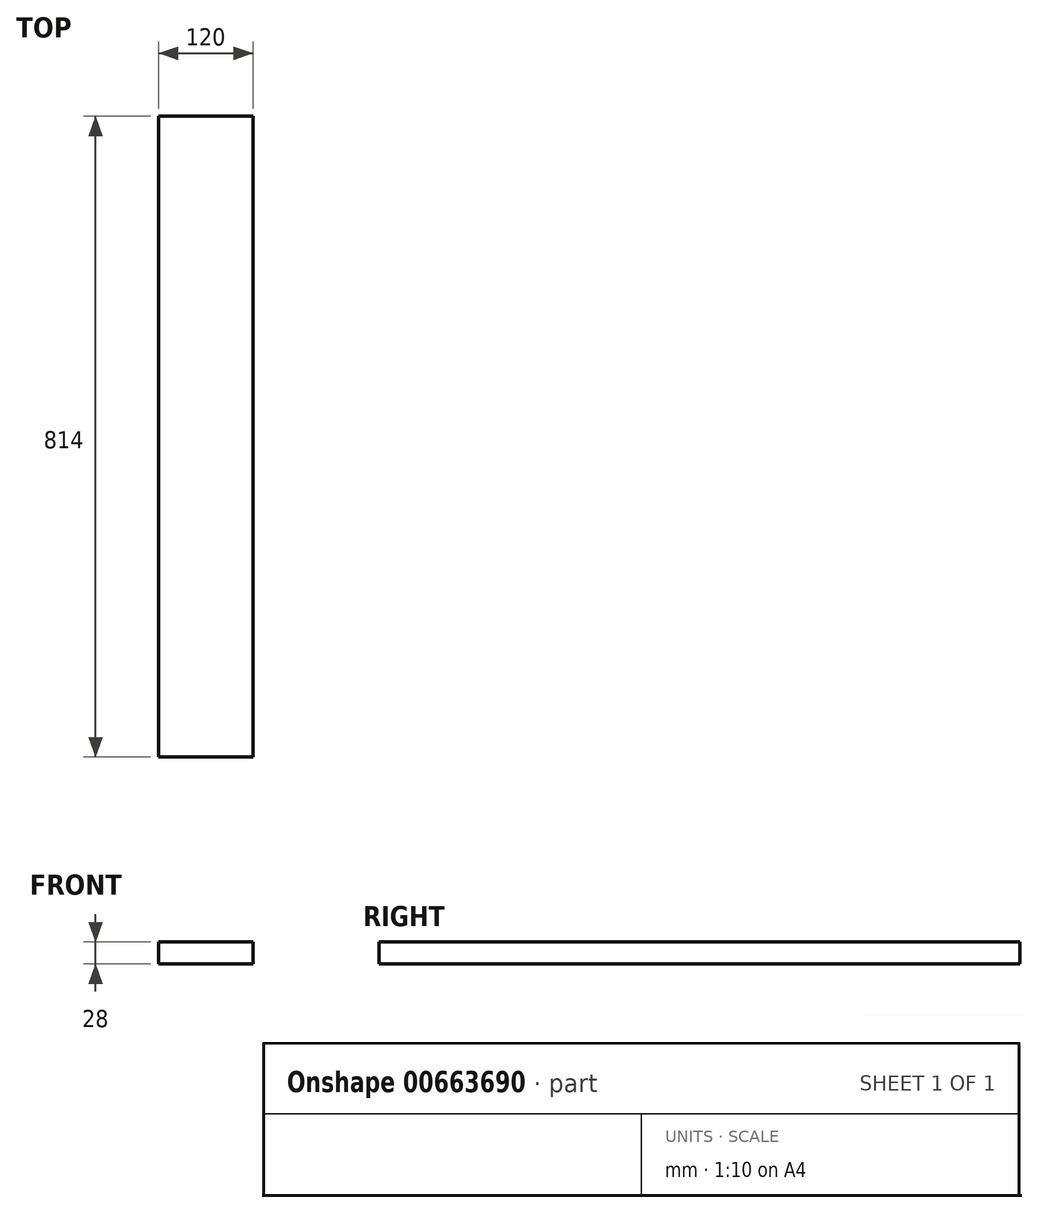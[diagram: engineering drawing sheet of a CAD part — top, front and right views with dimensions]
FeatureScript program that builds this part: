
annotation { "Feature Type Name" : "Feature", "Feature Type Description" : "" }
export const myFeature = defineFeature(function(context is Context, id is Id, definition is map)
    precondition{}
    {
        {
            var Q0;
            Q0=qCreatedBy(makeId("Front.planeOp"),FACE);
            var sketch = newSketch(context, id + "F0", { "sketchPlane" : qUnion([Q0])});
            skLineSegment(sketch, "E0.bottom", {"start": v(0, 0) * mm, "end": v(120, 0) * mm});
            skLineSegment(sketch, "E0.top", {"start": v(0, 28) * mm, "end": v(120, 28) * mm});
            skLineSegment(sketch, "E0.left", {"start": v(0, 0) * mm, "end": v(0, 28) * mm});
            skLineSegment(sketch, "E0.right", {"start": v(120, 0) * mm, "end": v(120, 28) * mm});
            skSolve(sketch);
        }
        {
            var Q0;
            Q0 = qSketchRegion(id + "F0", true);
            extrude(context, id + "F1", {"entities" : qUnion([Q0]), "depth" : 814 * mm, "offsetDistance" : 25 * mm});
        }
    });
